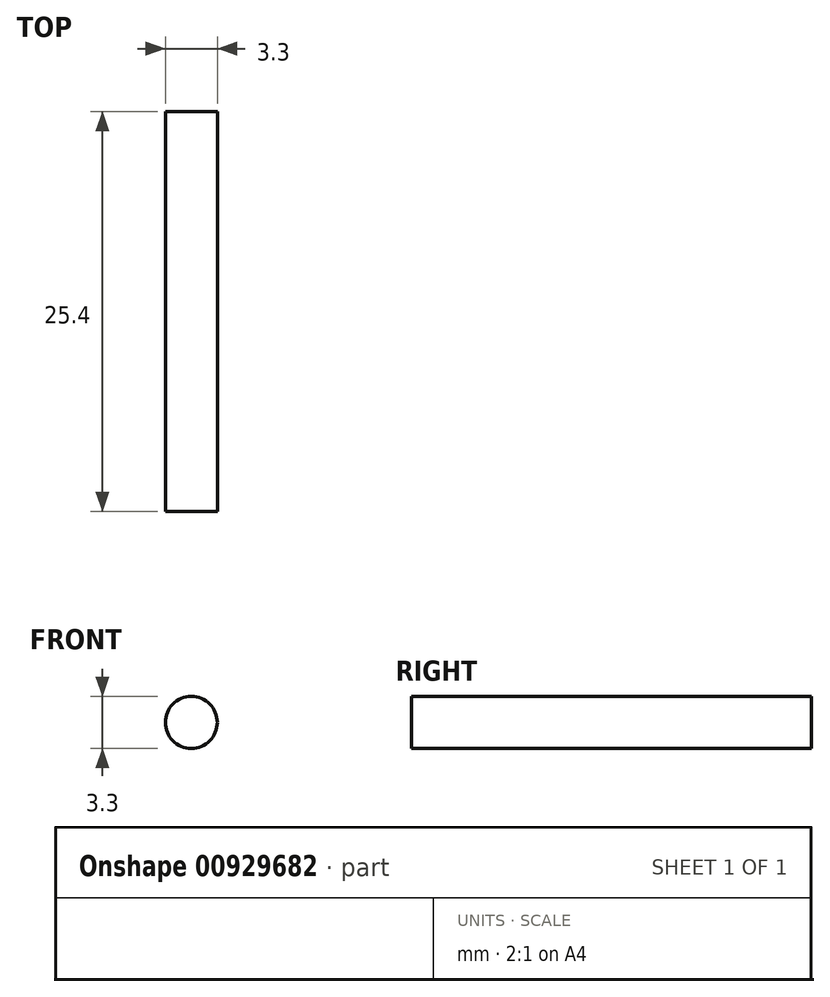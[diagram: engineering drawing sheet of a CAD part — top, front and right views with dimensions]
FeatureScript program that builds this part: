
annotation { "Feature Type Name" : "Feature", "Feature Type Description" : "" }
export const myFeature = defineFeature(function(context is Context, id is Id, definition is map)
    precondition{}
    {
        {
            var Q0;
            Q0=qCreatedBy(makeId("Front.planeOp"),FACE);
            var sketch = newSketch(context, id + "F0", { "sketchPlane" : qUnion([Q0])});
            skCircle(sketch, "E0", {"center": v(0, 0) * mm, "radius": 1.65 * mm});
            skSolve(sketch);
        }
        {
            var Q0;
            Q0=qSketchRegion(id+"F0",true);
            extrude(context, id + "F1", {"entities" : qUnion([Q0]), "depth" : 25.4 * mm, "offsetDistance" : 25.4 * mm});
        }
    });
